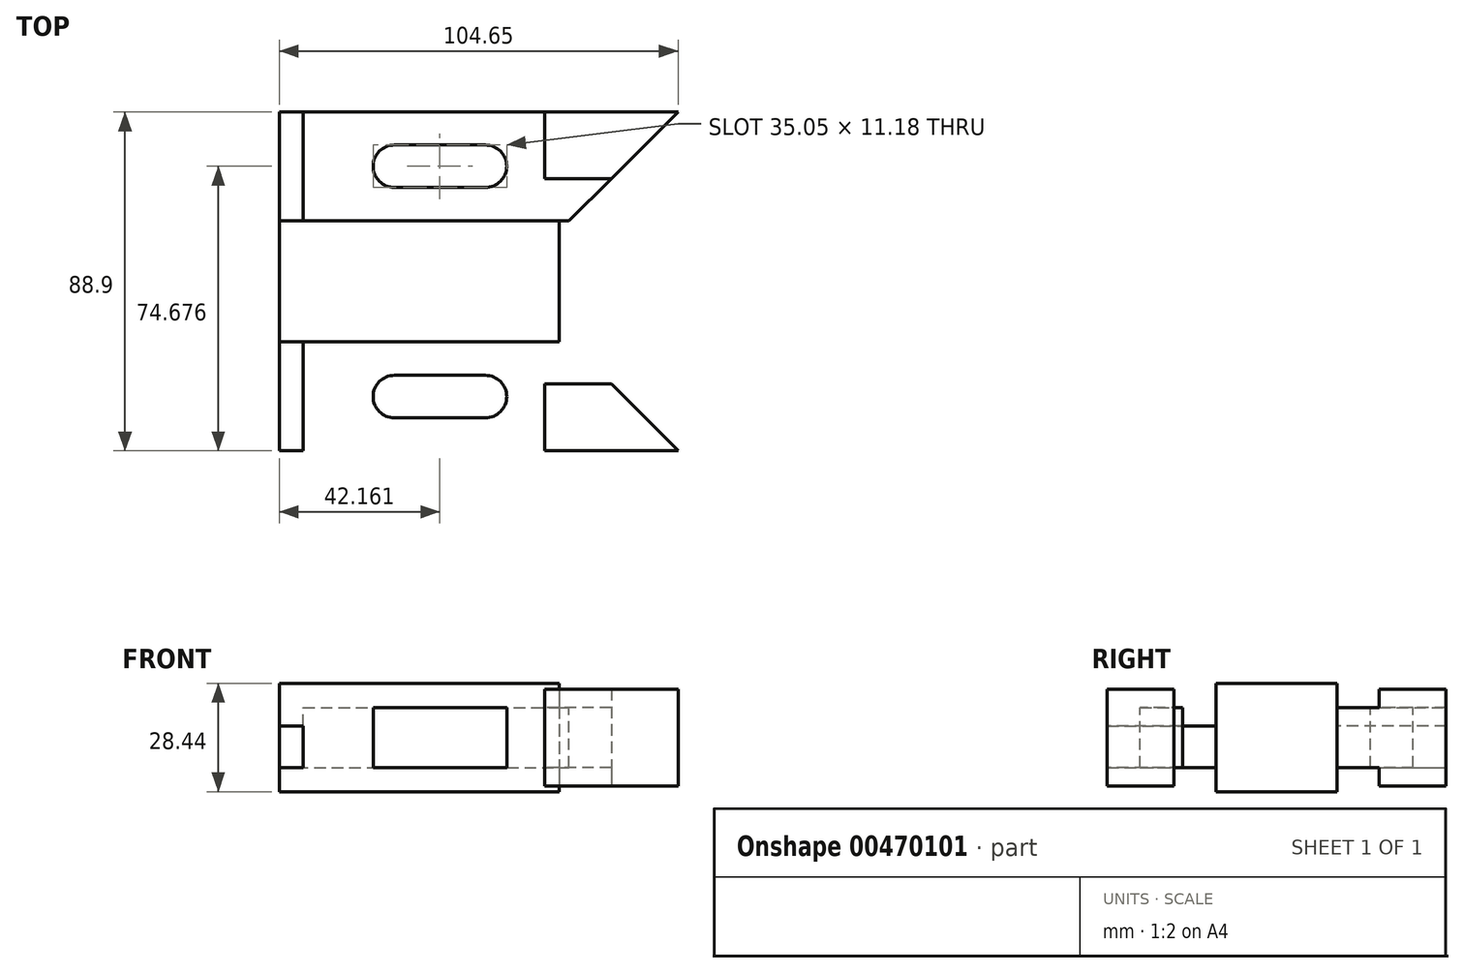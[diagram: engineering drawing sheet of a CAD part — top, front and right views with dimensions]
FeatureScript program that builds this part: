
annotation { "Feature Type Name" : "Feature", "Feature Type Description" : "" }
export const myFeature = defineFeature(function(context is Context, id is Id, definition is map)
    precondition{}
    {
        {
            var Q0;
            Q0=qCreatedBy(makeId("Top.planeOp"),FACE);
            var sketch = newSketch(context, id + "F0", { "sketchPlane" : qUnion([Q0])});
            skLineSegment(sketch, "E0.bottom", {"start": v(-36.7, 15.88) * mm, "end": v(36.7, 15.88) * mm});
            skLineSegment(sketch, "E0.top", {"start": v(-36.7, -15.88) * mm, "end": v(36.7, -15.88) * mm});
            skLineSegment(sketch, "E0.left", {"start": v(-36.7, 15.88) * mm, "end": v(-36.7, -15.87) * mm});
            skLineSegment(sketch, "E0.right", {"start": v(36.7, 15.88) * mm, "end": v(36.7, -15.87) * mm});
            skPoint(sketch, "E0.middle", {"position": v(0, 0) * mm});
            skLineSegment(sketch, "E1.bottom", {"start": v(-36.7, 15.88) * mm, "end": v(39.37, 15.88) * mm});
            skLineSegment(sketch, "E1.top", {"start": v(-36.7, 44.45) * mm, "end": v(67.95, 44.45) * mm});
            skLineSegment(sketch, "E1.left", {"start": v(-36.7, 15.88) * mm, "end": v(-36.7, 44.45) * mm});
            skLineSegment(sketch, "E2", {"start": v(67.95, 44.45) * mm, "end": v(39.37, 15.88) * mm});
            skLineSegment(sketch, "E3", {"start": v(50.42, 26.92) * mm, "end": v(32.9, 26.92) * mm});
            skLineSegment(sketch, "E4", {"start": v(32.9, 26.92) * mm, "end": v(32.9, 44.45) * mm});
            skLineSegment(sketch, "E5", {"start": v(-30.35, 44.45) * mm, "end": v(-30.35, 15.88) * mm});
            skArc(sketch, "E6", {"start": v(-6.48, 35.81) * mm, "mid": v(-12.07, 30.23) * mm, "end": v(-6.48, 24.64) * mm});
            skArc(sketch, "E7", {"start": v(17.4, 24.64) * mm, "mid": v(22.99, 30.23) * mm, "end": v(17.4, 35.81) * mm});
            skLineSegment(sketch, "E8", {"start": v(-6.48, 35.81) * mm, "end": v(17.4, 35.81) * mm});
            skLineSegment(sketch, "E9", {"start": v(-6.48, 24.64) * mm, "end": v(17.4, 24.64) * mm});
            skArc(sketch, "E10.MirrorCS", {"start": v(17.4, -24.64) * mm, "mid": v(22.99, -30.23) * mm, "end": v(17.4, -35.81) * mm});
            skLineSegment(sketch, "E11.MirrorCS", {"start": v(-6.48, -35.81) * mm, "end": v(17.4, -35.81) * mm});
            skArc(sketch, "E12.MirrorCS", {"start": v(-6.48, -35.81) * mm, "mid": v(-12.07, -30.23) * mm, "end": v(-6.48, -24.64) * mm});
            skLineSegment(sketch, "E13.MirrorCS", {"start": v(-6.48, -24.64) * mm, "end": v(17.4, -24.64) * mm});
            skLineSegment(sketch, "E14.MirrorCS", {"start": v(-30.35, -44.45) * mm, "end": v(-30.35, -15.88) * mm});
            skLineSegment(sketch, "E15.MirrorCS", {"start": v(-36.7, -44.45) * mm, "end": v(67.95, -44.45) * mm});
            skLineSegment(sketch, "E16.MirrorCS", {"start": v(-36.7, -15.88) * mm, "end": v(-36.7, -44.45) * mm});
            skLineSegment(sketch, "E17.MirrorCS", {"start": v(32.9, -26.92) * mm, "end": v(32.9, -44.45) * mm});
            skLineSegment(sketch, "E18.MirrorCS", {"start": v(50.42, -26.92) * mm, "end": v(32.9, -26.92) * mm});
            skLineSegment(sketch, "E19.MirrorCS", {"start": v(67.95, -44.45) * mm, "end": v(39.37, -15.88) * mm});
            skLineSegment(sketch, "E20.MirrorCS", {"start": v(-36.7, -15.88) * mm, "end": v(39.37, -15.88) * mm});
            skSolve(sketch);
        }
        {
            var Q0;
            {var subQ3=sQuery(id+"F0.wireOp",EDGE,"E0.left");Q0=makeQuery(id+"F0.imprint","IMPRINT",FACE,{"disambiguationData":[TD([[makeQuery(id+"F0.imprint","IMPRINT",EDGE,{"derivedFrom":subQ3}),1.0]])]});}
            extrude(context, id + "F1", {"entities" : qUnion([Q0]), "endBound" : BoundingType.SYMMETRIC, "depth" : 28.45 * mm});
        }
        {
            var Q0;
            {var subQ2=sQuery(id+"F0.wireOp",EDGE,"E3");Q0=makeQuery(id+"F0.imprint","IMPRINT",FACE,{"disambiguationData":[TD([[makeQuery(id+"F0.imprint","IMPRINT",EDGE,{"derivedFrom":subQ2}),1.0]])]});}
            var Q1;
            Q1=makeQuery(id+"F0.imprint","IMPRINT",FACE,{"disambiguationData":[TD([[makeQuery(id+"F0.imprint","IMPRINT",EDGE,{"derivedFrom":sQuery(id+"F0.wireOp",EDGE,"E10.MirrorCS")}),1.0]])]});
            extrude(context, id + "F2", {"entities" : qUnion([Q0, Q1]), "operationType" : NewBodyOperationType.ADD, "endBound" : BoundingType.SYMMETRIC, "oppositeDirection" : true, "depth" : 15.75 * mm});
        }
        {
            var Q0;
            {var subQ4=sQuery(id+"F0.wireOp",EDGE,"E3");Q0=makeQuery(id+"F0.imprint","IMPRINT",FACE,{"disambiguationData":[TD([[makeQuery(id+"F0.imprint","IMPRINT",EDGE,{"derivedFrom":subQ4}),-1.0]])]});}
            var Q1;
            {var subQ3=sQuery(id+"F0.wireOp",EDGE,"E17.MirrorCS");Q1=makeQuery(id+"F0.imprint","IMPRINT",FACE,{"disambiguationData":[TD([[makeQuery(id+"F0.imprint","IMPRINT",EDGE,{"derivedFrom":subQ3}),1.0]])]});}
            extrude(context, id + "F3", {"entities" : qUnion([Q0, Q1]), "operationType" : NewBodyOperationType.ADD, "endBound" : BoundingType.SYMMETRIC, "depth" : 25.4 * mm});
        }
        {
            var Q0;
            {var subQ0=sQuery(id+"F0.wireOp",EDGE,"E1.left");Q0=makeQuery(id+"F0.imprint","IMPRINT",FACE,{"disambiguationData":[TD([[makeQuery(id+"F0.imprint","IMPRINT",EDGE,{"derivedFrom":subQ0}),-1.0]])]});}
            var Q1;
            {var subQ0=sQuery(id+"F0.wireOp",EDGE,"E14.MirrorCS");Q1=makeQuery(id+"F0.imprint","IMPRINT",FACE,{"disambiguationData":[TD([[makeQuery(id+"F0.imprint","IMPRINT",EDGE,{"derivedFrom":subQ0}),1.0]])]});}
            extrude(context, id + "F4", {"entities" : qUnion([Q0, Q1]), "operationType" : NewBodyOperationType.ADD, "oppositeDirection" : true, "depth" : 7.87 * mm});
        }
        {
            var Q0;
            {var subQ0=sQuery(id+"F0.wireOp",EDGE,"E1.left");Q0=makeQuery(id+"F0.imprint","IMPRINT",FACE,{"disambiguationData":[TD([[makeQuery(id+"F0.imprint","IMPRINT",EDGE,{"derivedFrom":subQ0}),-1.0]])]});}
            var Q1;
            {var subQ0=sQuery(id+"F0.wireOp",EDGE,"E14.MirrorCS");Q1=makeQuery(id+"F0.imprint","IMPRINT",FACE,{"disambiguationData":[TD([[makeQuery(id+"F0.imprint","IMPRINT",EDGE,{"derivedFrom":subQ0}),1.0]])]});}
            extrude(context, id + "F5", {"entities" : qUnion([Q0, Q1]), "operationType" : NewBodyOperationType.ADD, "depth" : 3.05 * mm});
        }
    });
